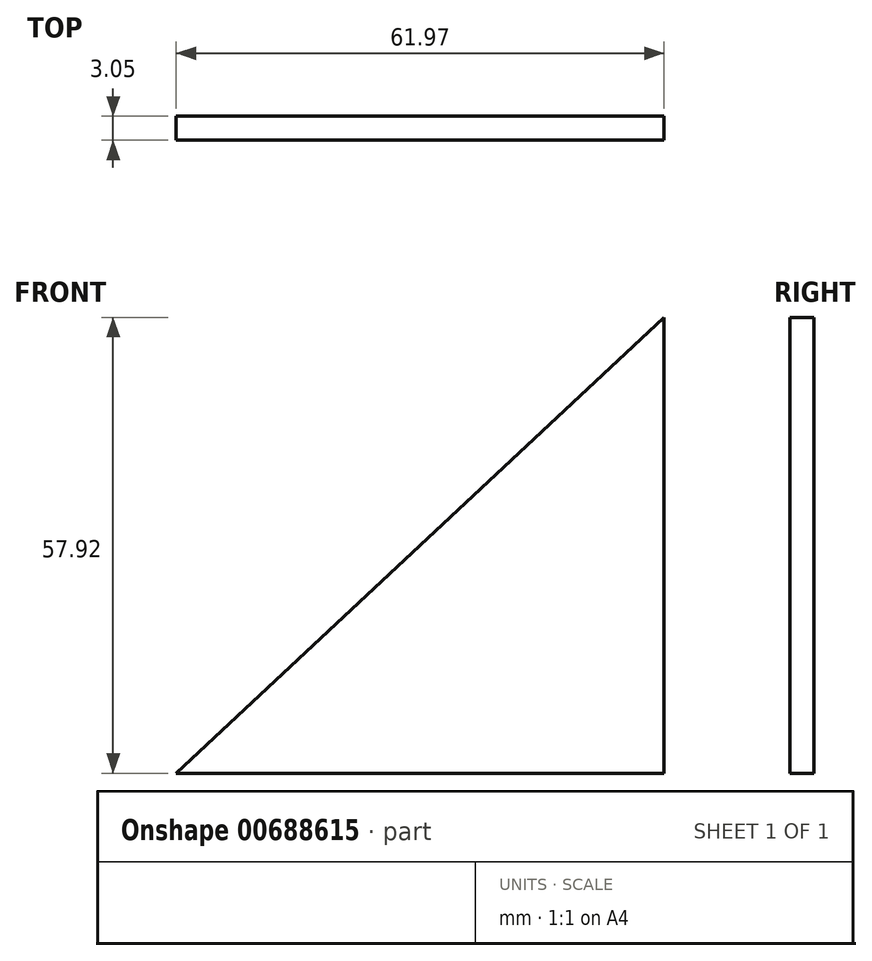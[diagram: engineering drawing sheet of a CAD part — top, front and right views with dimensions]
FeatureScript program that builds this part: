
annotation { "Feature Type Name" : "Feature", "Feature Type Description" : "" }
export const myFeature = defineFeature(function(context is Context, id is Id, definition is map)
    precondition{}
    {
        {
            var Q0;
            Q0=qCreatedBy(makeId("Front.planeOp"),FACE);
            var sketch = newSketch(context, id + "F0", { "sketchPlane" : qUnion([Q0])});
            skLineSegment(sketch, "E0", {"start": v(20.2, 33.9) * mm, "end": v(-41.78, -24) * mm});
            skLineSegment(sketch, "E1", {"start": v(-41.78, -24) * mm, "end": v(20.2, -24) * mm});
            skLineSegment(sketch, "E2", {"start": v(20.2, -24) * mm, "end": v(20.2, 33.9) * mm});
            skSolve(sketch);
        }
        {
            var Q0;
            Q0=makeQuery(id+"F0.imprint","IMPRINT",FACE,{"disambiguationData":[TD([[makeQuery(id+"F0.imprint","IMPRINT",EDGE,{"derivedFrom":sQuery(id+"F0.wireOp",EDGE,"E0")}),1.0]])]});
            extrude(context, id + "F1", {"entities" : qUnion([Q0]), "depth" : 3.05 * mm, "offsetDistance" : 25.4 * mm});
        }
    });
